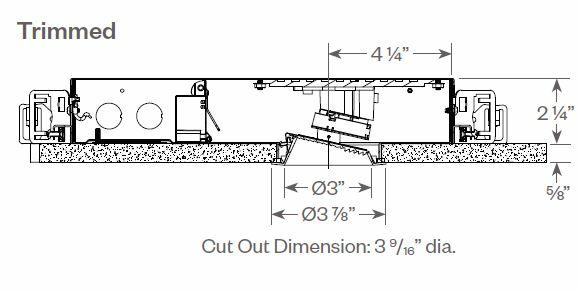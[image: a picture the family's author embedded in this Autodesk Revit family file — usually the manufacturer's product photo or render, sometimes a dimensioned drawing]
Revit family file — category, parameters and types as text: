
# Revit family: Lighting-Recessed-Amerlux-Solace Round Wallwash
name_source: partatom
category: Lighting Fixtures
revit_build: Autodesk Revit 2017 (Build: 20190508_0315(x64)
units: mm (PartAtom-declared; Revit-internal decimal feet)

## family parameters
Cut with Voids When Loaded = No
Host = Face
Light Source = Yes
Part Type = Normal
Room Calculation Point = No
Round Connector Dimension = Use Diameter
Shared = No

## types (2) — shared parameters
Aperture Size = 3"
Apparent Load = 0 VA
Color Filter = 16777215
Default Elevation = 48"
Dimming Lamp Color Temperature Shift = <None>
Emit Shape Visible in Rendering = No
Emit from Circle Diameter = 3"
Height = 2 1/4"
Lamp = LED
Length = 16 1/2"
Manufacturer = Amerlux
Number of Poles = 1
Photometric Web File = Load File
Power Factor = 1
Tilt Angle = -90.00°
Trim Size = 3 7/8"
URL = http://www.amerlux.com
Voltage = 0 V
Width = 8"

## per-type parameters (varying)
| type | Description | Model |
| Downlight | Shallow Round Adjustable | SOL-RD |
| Wallwash | Shallow Round Wallwash | SOL-RLW |

## geometry (parser evidence)
native form markers: Blend x10, Sweep x2
no freeform markers — native parametric forms only
